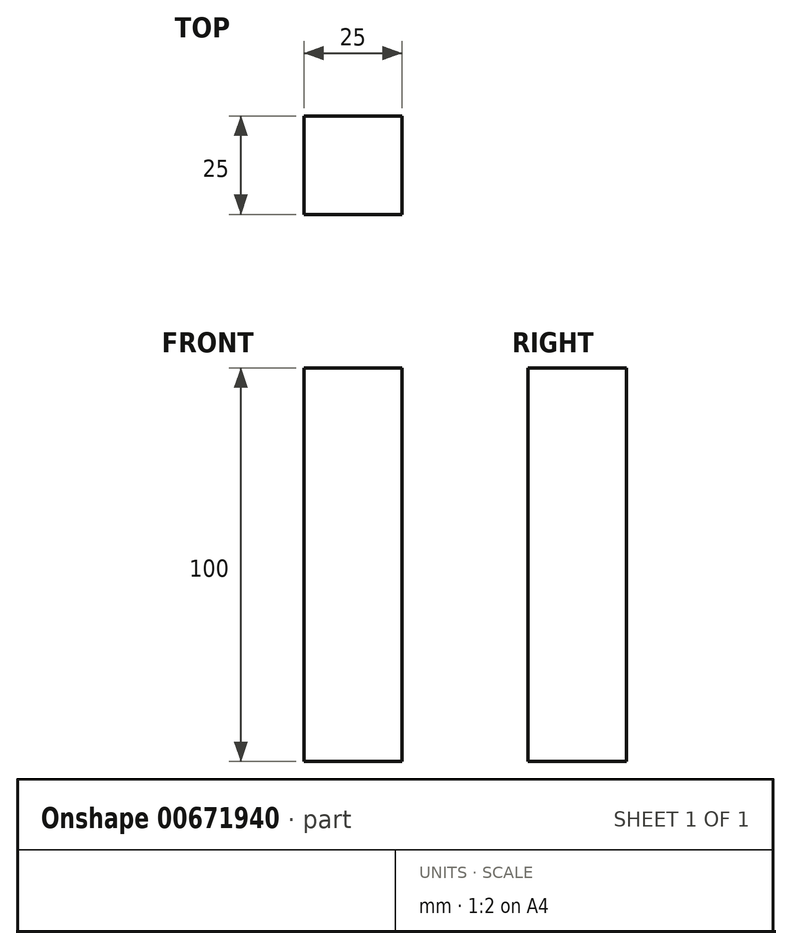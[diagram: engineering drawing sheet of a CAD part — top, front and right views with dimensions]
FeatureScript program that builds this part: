
annotation { "Feature Type Name" : "Feature", "Feature Type Description" : "" }
export const myFeature = defineFeature(function(context is Context, id is Id, definition is map)
    precondition{}
    {
        {
            var Q0;
            Q0=qCreatedBy(makeId("Front.planeOp"),FACE);
            var sketch = newSketch(context, id + "F0", { "sketchPlane" : qUnion([Q0])});
            skLineSegment(sketch, "E0.bottom", {"start": v(-47.88, 57.2) * mm, "end": v(-22.88, 57.2) * mm});
            skLineSegment(sketch, "E0.top", {"start": v(-47.88, -42.8) * mm, "end": v(-22.88, -42.8) * mm});
            skLineSegment(sketch, "E0.left", {"start": v(-47.88, 57.2) * mm, "end": v(-47.88, -42.8) * mm});
            skLineSegment(sketch, "E0.right", {"start": v(-22.88, 57.2) * mm, "end": v(-22.88, -42.8) * mm});
            skSolve(sketch);
        }
        {
            var Q0;
            Q0 = qSketchRegion(id + "F0", true);
            extrude(context, id + "F1", {"entities" : qUnion([Q0]), "depth" : 25 * mm, "offsetDistance" : 25 * mm});
        }
    });
